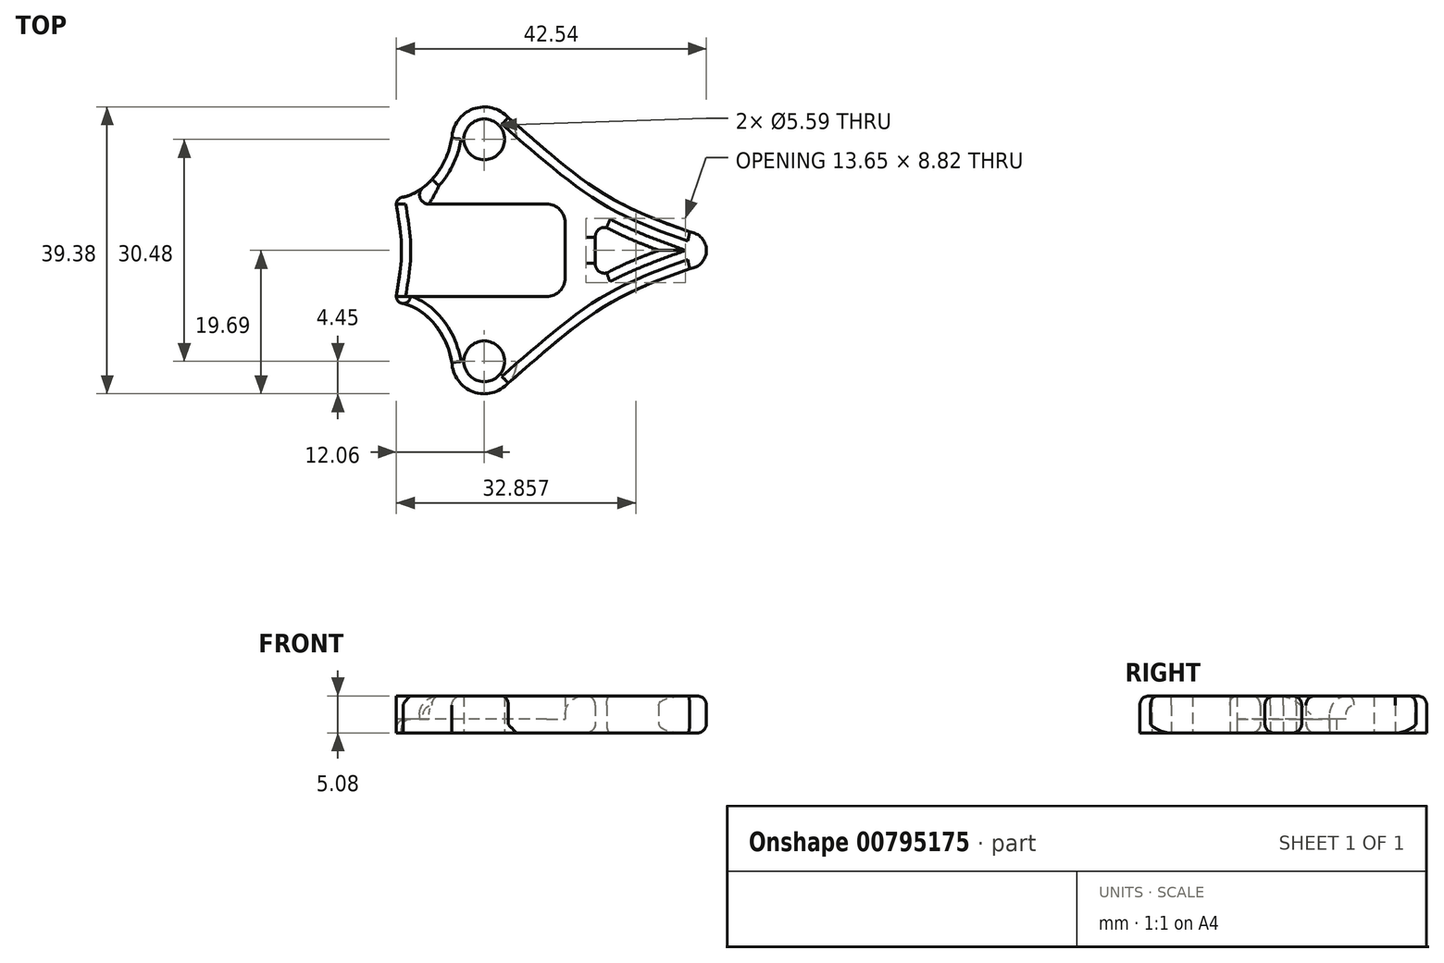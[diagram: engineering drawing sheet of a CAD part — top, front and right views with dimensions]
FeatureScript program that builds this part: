
annotation { "Feature Type Name" : "Feature", "Feature Type Description" : "" }
export const myFeature = defineFeature(function(context is Context, id is Id, definition is map)
    precondition{}
    {
        {
            var Q0;
            Q0=qCreatedBy(makeId("Top.planeOp"),FACE);
            var sketch = newSketch(context, id + "F0", { "sketchPlane" : qUnion([Q0])});
            skLineSegment(sketch, "E0", {"start": v(0, 0) * mm, "end": v(0, 15.24) * mm, "construction": true});
            skCircle(sketch, "E1", {"center": v(0, 15.24) * mm, "radius": 2.8 * mm});
            skCircle(sketch, "E2", {"center": v(0, -15.24) * mm, "radius": 2.8 * mm});
            skArc(sketch, "E3", {"start": v(3.3, 18.22) * mm, "mid": v(-1.53, 19.41) * mm, "end": v(-4.44, 15.39) * mm});
            skArc(sketch, "E4", {"start": v(-4.44, -15.39) * mm, "mid": v(-1.53, -19.41) * mm, "end": v(3.3, -18.22) * mm});
            skLineSegment(sketch, "E5", {"start": v(0, 0) * mm, "end": v(15.24, 0) * mm, "construction": true});
            skLineSegment(sketch, "E6", {"start": v(15.24, 0) * mm, "end": v(27.94, 0) * mm, "construction": true});
            skArc(sketch, "E7", {"start": v(28.19, -2.53) * mm, "mid": v(30.48, 0) * mm, "end": v(28.19, 2.53) * mm});
            skFitSpline(sketch, "E8", {"points": [v(3.3, -18.22) * mm, v(28.19, -2.53) * mm], "startDerivative": vector(34.18, 29.84) * mm, "endDerivative": vector(33.4, 11.86) * mm});
            skFitSpline(sketch, "E9.MirrorCS", {"points": [v(3.3, 18.22) * mm, v(28.19, 2.53) * mm], "startDerivative": vector(34.18, -29.84) * mm, "endDerivative": vector(33.4, -11.86) * mm});
            skArc(sketch, "E10", {"start": v(21.03, -1.17) * mm, "mid": v(21.81, 0) * mm, "end": v(21.03, 1.17) * mm});
            skArc(sketch, "E11", {"start": v(17.1, 3) * mm, "mid": v(15.82, 2.94) * mm, "end": v(15.24, 1.8) * mm});
            skArc(sketch, "E12", {"start": v(15.24, -1.79) * mm, "mid": v(15.81, -2.94) * mm, "end": v(17.1, -3) * mm});
            skFitSpline(sketch, "E13.trimOffspring", {"points": [v(0.8, 15.35) * mm, v(2.22, 14.1) * mm, v(4.8, 11.86) * mm, v(8.08, 9.1) * mm, v(11, 6.8) * mm, v(13.78, 4.87) * mm, v(16.6, 3.22) * mm, v(19.6, 1.76) * mm, v(22.92, 0.38) * mm, v(25.5, -0.56) * mm, v(26.91, -1.06) * mm]});
            skFitSpline(sketch, "E14.trimOffspring", {"points": [v(0.8, -15.35) * mm, v(2.22, -14.1) * mm, v(4.8, -11.86) * mm, v(8.08, -9.1) * mm, v(11, -6.8) * mm, v(13.78, -4.87) * mm, v(16.6, -3.22) * mm, v(19.6, -1.76) * mm, v(22.92, -0.38) * mm, v(25.5, 0.56) * mm, v(26.91, 1.06) * mm]});
            skLineSegment(sketch, "E15", {"start": v(15.24, 1.94) * mm, "end": v(15.24, -1.96) * mm});
            skLineSegment(sketch, "E16.bottom", {"start": v(11.11, -6.35) * mm, "end": v(-11.11, -6.35) * mm});
            skLineSegment(sketch, "E16.top", {"start": v(11.11, 6.35) * mm, "end": v(-11.11, 6.35) * mm});
            skLineSegment(sketch, "E16.left", {"start": v(11.11, -6.35) * mm, "end": v(11.11, 6.35) * mm});
            skPoint(sketch, "E16.middle", {"position": v(0, 0) * mm});
            skArc(sketch, "E17", {"start": v(-11.11, 7.3) * mm, "mid": v(-11.78, 7.02) * mm, "end": v(-12.06, 6.35) * mm});
            skArc(sketch, "E18", {"start": v(-12.06, -6.35) * mm, "mid": v(-11.79, -7.02) * mm, "end": v(-11.11, -7.3) * mm});
            skFitSpline(sketch, "E19", {"points": [v(-4.44, 15.39) * mm, v(-11.11, 7.3) * mm], "startDerivative": vector(-2.37, -13.26) * mm, "endDerivative": vector(-8.72, -2.02) * mm});
            skFitSpline(sketch, "E20.MirrorCS", {"points": [v(-4.44, -15.39) * mm, v(-11.11, -7.3) * mm], "startDerivative": vector(-2.37, 13.26) * mm, "endDerivative": vector(-8.72, 2.02) * mm});
            skFitSpline(sketch, "E21", {"points": [v(-12.06, 6.35) * mm, v(-12.06, -6.35) * mm], "startDerivative": vector(2.86, -19.06) * mm, "endDerivative": vector(-2.86, -19.05) * mm});
            skLineSegment(sketch, "E22", {"start": v(-11.11, 6.35) * mm, "end": v(-12.06, 6.35) * mm});
            skLineSegment(sketch, "E23", {"start": v(-11.11, -6.35) * mm, "end": v(-12.06, -6.35) * mm});
            skSolve(sketch);
        }
        {
            var Q0;
            Q0=makeQuery(id+"F0.imprint","IMPRINT",FACE,{"disambiguationData":[TD([[makeQuery(id+"F0.imprint","IMPRINT",EDGE,{"derivedFrom":sQuery(id+"F0.wireOp",EDGE,"E1")}),-1.0]])]});
            extrude(context, id + "F1", {"entities" : qUnion([Q0]), "depth" : 5.08 * mm, "offsetDistance" : 25.4 * mm});
        }
        {
            var Q0;
            Q0=makeQuery(id+"F0.imprint","IMPRINT",FACE,{"disambiguationData":[TD([[makeQuery(id+"F0.imprint","IMPRINT",EDGE,{"derivedFrom":sQuery(id+"F0.wireOp",EDGE,"E16.bottom")}),-1.0]])]});
            extrude(context, id + "F2", {"entities" : qUnion([Q0]), "operationType" : NewBodyOperationType.ADD, "depth" : 1.9 * mm, "offsetDistance" : 25.4 * mm});
        }
        {
            var Q0;
            Q0=makeQuery(id+"F1.opExtrude","SWEPT_EDGE",EDGE,{"disambiguationData":[OSD([sQuery(id+"F0.wireOp",EDGE,"E16.top"),sQuery(id+"F0.wireOp",EDGE,"E16.left")])]});
            var Q1;
            Q1=makeQuery(id+"F1.opExtrude","SWEPT_EDGE",EDGE,{"disambiguationData":[OSD([sQuery(id+"F0.wireOp",EDGE,"E16.bottom"),sQuery(id+"F0.wireOp",EDGE,"E16.left")])]});
            var Q2;
            Q2=makeQuery(id+"F1.opExtrude","CAP_EDGE",EDGE,{"disambiguationData":[OSD([sQuery(id+"F0.wireOp",EDGE,"E16.top")])],"isStart":false});
            fillet(context, id + "F3", {"entities" : qUnion([Q0, Q1, Q2]), "radius" : 2.54 * mm, "tangentPropagation" : true, "allowEdgeOverflow" : false});
        }
        {
            var Q0;
            Q0=makeQuery(id+"F2.opExtrude","CAP_EDGE",EDGE,{"disambiguationData":[OSD([sQuery(id+"F0.wireOp",EDGE,"E21")])],"isStart":false});
            fillet(context, id + "F4", {"entities" : qUnion([Q0]), "radius" : 1.27 * mm, "tangentPropagation" : true, "allowEdgeOverflow" : false});
        }
        {
            var Q0;
            Q0=makeQuery(id+"F1.opExtrude","CAP_EDGE",EDGE,{"disambiguationData":[OSD([sQuery(id+"F0.wireOp",EDGE,"E13.trimOffspring")])],"isStart":false});
            var Q1;
            Q1=makeQuery(id+"F1.opExtrude","CAP_EDGE",EDGE,{"disambiguationData":[OSD([sQuery(id+"F0.wireOp",EDGE,"E14.trimOffspring")])],"isStart":false});
            var Q2;
            Q2=makeQuery(id+"F1.opExtrude","CAP_EDGE",EDGE,{"disambiguationData":[OSD([sQuery(id+"F0.wireOp",EDGE,"E12")])],"isStart":false});
            var Q3;
            Q3=makeQuery(id+"F1.opExtrude","CAP_EDGE",EDGE,{"disambiguationData":[OSD([sQuery(id+"F0.wireOp",EDGE,"E11")])],"isStart":false});
            var Q4;
            Q4=makeQuery(id+"F1.opExtrude","CAP_EDGE",EDGE,{"disambiguationData":[OSD([sQuery(id+"F0.wireOp",EDGE,"E15")])],"isStart":false});
            var Q5;
            Q5=makeQuery(id+"F1.opExtrude","CAP_EDGE",EDGE,{"disambiguationData":[OSD([sQuery(id+"F0.wireOp",EDGE,"E10")])],"isStart":false});
            var Q6;
            Q6=makeQuery(id+"F1.opExtrude","CAP_EDGE",EDGE,{"disambiguationData":[OSD([sQuery(id+"F0.wireOp",EDGE,"E14.trimOffspring")])],"isStart":true});
            var Q7;
            Q7=makeQuery(id+"F1.opExtrude","CAP_EDGE",EDGE,{"disambiguationData":[OSD([sQuery(id+"F0.wireOp",EDGE,"E12")])],"isStart":true});
            var Q8;
            Q8=makeQuery(id+"F1.opExtrude","CAP_EDGE",EDGE,{"disambiguationData":[OSD([sQuery(id+"F0.wireOp",EDGE,"E10")])],"isStart":true});
            var Q9;
            Q9=makeQuery(id+"F1.opExtrude","CAP_EDGE",EDGE,{"disambiguationData":[OSD([sQuery(id+"F0.wireOp",EDGE,"E13.trimOffspring")])],"isStart":true});
            var Q10;
            Q10=makeQuery(id+"F1.opExtrude","CAP_EDGE",EDGE,{"disambiguationData":[OSD([sQuery(id+"F0.wireOp",EDGE,"E11")])],"isStart":true});
            var Q11;
            Q11=makeQuery(id+"F1.opExtrude","CAP_EDGE",EDGE,{"disambiguationData":[OSD([sQuery(id+"F0.wireOp",EDGE,"E15")])],"isStart":true});
            var Q12;
            Q12=makeQuery(id+"F1.opExtrude","CAP_EDGE",EDGE,{"disambiguationData":[OSD([sQuery(id+"F0.wireOp",EDGE,"E8")])],"isStart":false});
            var Q13;
            Q13=makeQuery(id+"F1.opExtrude","CAP_EDGE",EDGE,{"disambiguationData":[OSD([sQuery(id+"F0.wireOp",EDGE,"E7")])],"isStart":false});
            var Q14;
            Q14=makeQuery(id+"F1.opExtrude","CAP_EDGE",EDGE,{"disambiguationData":[OSD([sQuery(id+"F0.wireOp",EDGE,"E9.MirrorCS")])],"isStart":false});
            var Q15;
            Q15=makeQuery(id+"F1.opExtrude","CAP_EDGE",EDGE,{"disambiguationData":[OSD([sQuery(id+"F0.wireOp",EDGE,"E3")])],"isStart":false});
            var Q16;
            Q16=makeQuery(id+"F1.opExtrude","CAP_EDGE",EDGE,{"disambiguationData":[OSD([sQuery(id+"F0.wireOp",EDGE,"E19")])],"isStart":false});
            var Q17;
            Q17=makeQuery(id+"F1.opExtrude","CAP_EDGE",EDGE,{"disambiguationData":[OSD([sQuery(id+"F0.wireOp",EDGE,"E4")])],"isStart":false});
            var Q18;
            Q18=makeQuery(id+"F1.opExtrude","CAP_EDGE",EDGE,{"disambiguationData":[OSD([sQuery(id+"F0.wireOp",EDGE,"E20.MirrorCS")])],"isStart":false});
            var Q19;
            Q19=makeQuery(id+"F1.opExtrude","CAP_EDGE",EDGE,{"disambiguationData":[OSD([sQuery(id+"F0.wireOp",EDGE,"E8")])],"isStart":true});
            var Q20;
            Q20=makeQuery(id+"F1.opExtrude","CAP_EDGE",EDGE,{"disambiguationData":[OSD([sQuery(id+"F0.wireOp",EDGE,"E7")])],"isStart":true});
            var Q21;
            Q21=makeQuery(id+"F1.opExtrude","CAP_EDGE",EDGE,{"disambiguationData":[OSD([sQuery(id+"F0.wireOp",EDGE,"E9.MirrorCS")])],"isStart":true});
            fillet(context, id + "F5", {"entities" : qUnion([Q0, Q1, Q2, Q3, Q4, Q5, Q6, Q7, Q8, Q9, Q10, Q11, Q12, Q13, Q14, Q15, Q16, Q17, Q18, Q19, Q20, Q21]), "radius" : 1.27 * mm, "tangentPropagation" : true, "allowEdgeOverflow" : false});
        }
    });
